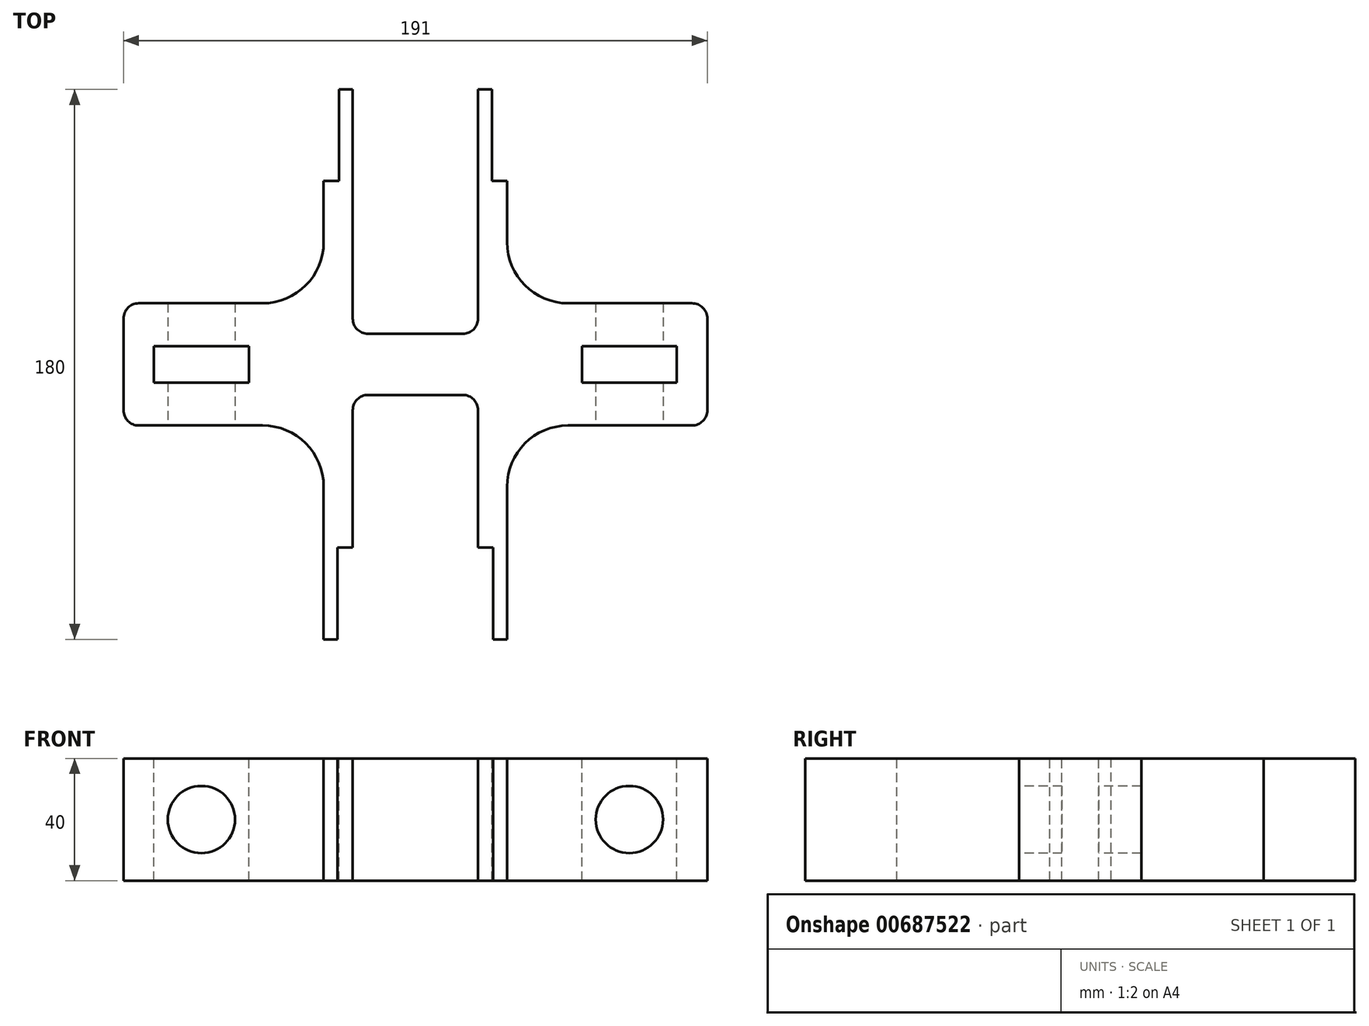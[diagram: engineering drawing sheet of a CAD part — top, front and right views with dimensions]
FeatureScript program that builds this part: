
annotation { "Feature Type Name" : "Feature", "Feature Type Description" : "" }
export const myFeature = defineFeature(function(context is Context, id is Id, definition is map)
    precondition{}
    {
        {
            var Q0;
            Q0=qCreatedBy(makeId("Front.planeOp"),FACE);
            var sketch = newSketch(context, id + "F0", { "sketchPlane" : qUnion([Q0])});
            skLineSegment(sketch, "E0.bottom", {"start": v(30, 20) * mm, "end": v(-30, 20) * mm});
            skLineSegment(sketch, "E0.top", {"start": v(30, -20) * mm, "end": v(-30, -20) * mm});
            skLineSegment(sketch, "E0.left", {"start": v(30, 20) * mm, "end": v(30, -20) * mm});
            skLineSegment(sketch, "E0.right", {"start": v(-30, 20) * mm, "end": v(-30, -20) * mm});
            skPoint(sketch, "E0.middle", {"position": v(0, 0) * mm});
            skSolve(sketch);
        }
        {
            var Q0;
            Q0 = qSketchRegion(id + "F0", true);
            extrude(context, id + "F1", {"entities" : qUnion([Q0]), "endBound" : BoundingType.SYMMETRIC, "depth" : 180 * mm, "offsetDistance" : 25 * mm});
        }
        {
            var Q0;
            Q0=makeQuery(id+"F1.opExtrude","CAP_FACE",FACE,{"disambiguationData":[OSD([sQuery(id+"F0.wireOp",EDGE,"E0.bottom"),sQuery(id+"F0.wireOp",EDGE,"E0.top"),sQuery(id+"F0.wireOp",EDGE,"E0.left"),sQuery(id+"F0.wireOp",EDGE,"E0.right")])],"isStart":false});
            var sketch = newSketch(context, id + "F2", { "sketchPlane" : qUnion([Q0])});
            skLineSegment(sketch, "E1.bottom", {"start": v(20.5, -20) * mm, "end": v(-20.5, -20) * mm});
            skLineSegment(sketch, "E1.top", {"start": v(20.5, 20) * mm, "end": v(-20.5, 20) * mm});
            skLineSegment(sketch, "E1.left", {"start": v(20.5, -20) * mm, "end": v(20.5, 20) * mm});
            skLineSegment(sketch, "E1.right", {"start": v(-20.5, -20) * mm, "end": v(-20.5, 20) * mm});
            skPoint(sketch, "E1.middle", {"position": v(0, 0) * mm});
            skSolve(sketch);
        }
        {
            var Q0;
            Q0 = qSketchRegion(id + "F2", true);
            extrude(context, id + "F3", {"entities" : qUnion([Q0]), "operationType" : NewBodyOperationType.REMOVE, "oppositeDirection" : true, "depth" : 80 * mm, "offsetDistance" : 25 * mm});
        }
        {
            var Q0;
            Q0=makeQuery(id+"F1.opExtrude","CAP_FACE",FACE,{"disambiguationData":[OSD([sQuery(id+"F0.wireOp",EDGE,"E0.bottom"),sQuery(id+"F0.wireOp",EDGE,"E0.top"),sQuery(id+"F0.wireOp",EDGE,"E0.left"),sQuery(id+"F0.wireOp",EDGE,"E0.right")])],"isStart":true});
            var sketch = newSketch(context, id + "F4", { "sketchPlane" : qUnion([Q0])});
            skLineSegment(sketch, "E2.bottom", {"start": v(-20.5, 20) * mm, "end": v(20.5, 20) * mm});
            skLineSegment(sketch, "E2.top", {"start": v(-20.5, -20) * mm, "end": v(20.5, -20) * mm});
            skLineSegment(sketch, "E2.left", {"start": v(-20.5, 20) * mm, "end": v(-20.5, -20) * mm});
            skLineSegment(sketch, "E2.right", {"start": v(20.5, 20) * mm, "end": v(20.5, -20) * mm});
            skPoint(sketch, "E2.middle", {"position": v(0, 0) * mm});
            skSolve(sketch);
        }
        {
            var Q0;
            Q0 = qSketchRegion(id + "F4", true);
            extrude(context, id + "F5", {"entities" : qUnion([Q0]), "operationType" : NewBodyOperationType.REMOVE, "oppositeDirection" : true, "depth" : 80 * mm, "offsetDistance" : 25 * mm});
        }
        {
            var Q0;
            Q0=qCreatedBy(makeId("Front.planeOp"),FACE);
            var sketch = newSketch(context, id + "F6", { "sketchPlane" : qUnion([Q0])});
            skPoint(sketch, "E3", {"position": v(70, 0) * mm});
            skLineSegment(sketch, "E4.bottom", {"start": v(20.5, -20) * mm, "end": v(95.5, -20) * mm});
            skLineSegment(sketch, "E4.top", {"start": v(20.5, 20) * mm, "end": v(95.5, 20) * mm});
            skLineSegment(sketch, "E4.left", {"start": v(20.5, -20) * mm, "end": v(20.5, 20) * mm});
            skLineSegment(sketch, "E4.right", {"start": v(95.5, -20) * mm, "end": v(95.5, 20) * mm});
            skLineSegment(sketch, "E5.bottom", {"start": v(-20.5, -20) * mm, "end": v(-95.5, -20) * mm});
            skLineSegment(sketch, "E5.top", {"start": v(-20.5, 20) * mm, "end": v(-95.5, 20) * mm});
            skLineSegment(sketch, "E5.left", {"start": v(-20.5, -20) * mm, "end": v(-20.5, 20) * mm});
            skLineSegment(sketch, "E5.right", {"start": v(-95.5, -20) * mm, "end": v(-95.5, 20) * mm});
            skPoint(sketch, "E6", {"position": v(-70, 0) * mm});
            skCircle(sketch, "E7", {"center": v(70, 0) * mm, "radius": 11 * mm});
            skCircle(sketch, "E8", {"center": v(-70, 0) * mm, "radius": 11 * mm});
            skSolve(sketch);
        }
        {
            var Q0;
            Q0 = qSketchRegion(id + "F6", true);
            extrude(context, id + "F7", {"entities" : qUnion([Q0]), "operationType" : NewBodyOperationType.ADD, "endBound" : BoundingType.SYMMETRIC, "oppositeDirection" : true, "depth" : 40 * mm, "offsetDistance" : 25 * mm});
        }
        {
            var Q0;
            Q0=makeQuery(id+"F7.boolean.opBoolean","MERGE",FACE,{"derivedFrom":[makeQuery(id+"F1.opExtrude","SWEPT_FACE",FACE,{"disambiguationData":[OSD([sQuery(id+"F0.wireOp",EDGE,"E0.bottom")])]}),makeQuery(id+"F7.opExtrude","SWEPT_FACE",FACE,{"disambiguationData":[OSD([sQuery(id+"F6.wireOp",EDGE,"E4.top")])]}),makeQuery(id+"F7.opExtrude","SWEPT_FACE",FACE,{"disambiguationData":[OSD([sQuery(id+"F6.wireOp",EDGE,"E5.top")])]})]});
            var sketch = newSketch(context, id + "F8", { "sketchPlane" : qUnion([Q0])});
            skLineSegment(sketch, "E9.bottom", {"start": v(-54.5, -6) * mm, "end": v(-85.5, -6) * mm});
            skLineSegment(sketch, "E9.top", {"start": v(-54.5, 6) * mm, "end": v(-85.5, 6) * mm});
            skLineSegment(sketch, "E9.left", {"start": v(-54.5, -6) * mm, "end": v(-54.5, 6) * mm});
            skLineSegment(sketch, "E9.right", {"start": v(-85.5, -6) * mm, "end": v(-85.5, 6) * mm});
            skPoint(sketch, "E9.middle", {"position": v(-70, 0) * mm});
            skLineSegment(sketch, "E10.bottom", {"start": v(85.5, -6) * mm, "end": v(54.5, -6) * mm});
            skLineSegment(sketch, "E10.top", {"start": v(85.5, 6) * mm, "end": v(54.5, 6) * mm});
            skLineSegment(sketch, "E10.left", {"start": v(85.5, -6) * mm, "end": v(85.5, 6) * mm});
            skLineSegment(sketch, "E10.right", {"start": v(54.5, -6) * mm, "end": v(54.5, 6) * mm});
            skPoint(sketch, "E10.middle", {"position": v(70, 0) * mm});
            skSolve(sketch);
        }
        {
            var Q0;
            Q0=makeQuery(id+"F8.imprint","IMPRINT",FACE,{"disambiguationData":[TD([[makeQuery(id+"F8.imprint","IMPRINT",EDGE,{"derivedFrom":sQuery(id+"F8.wireOp",EDGE,"E10.bottom")}),-1.0]])]});
            var Q1;
            Q1=makeQuery(id+"F8.imprint","IMPRINT",FACE,{"disambiguationData":[TD([[makeQuery(id+"F8.imprint","IMPRINT",EDGE,{"derivedFrom":sQuery(id+"F8.wireOp",EDGE,"E9.bottom")}),-1.0]])]});
            extrude(context, id + "F9", {"entities" : qUnion([Q0, Q1]), "operationType" : NewBodyOperationType.REMOVE, "oppositeDirection" : true, "depth" : 40 * mm, "offsetDistance" : 25 * mm});
        }
        {
            var Q0;
            Q0=makeQuery(id+"F7.boolean.opBoolean","INTERSECT",EDGE,{"derivedFrom":[makeQuery(id+"F1.opExtrude","SWEPT_FACE",FACE,{"disambiguationData":[OSD([sQuery(id+"F0.wireOp",EDGE,"E0.right")])]}),makeQuery(id+"F7.opExtrude","CAP_FACE",FACE,{"disambiguationData":[OSD([sQuery(id+"F6.wireOp",EDGE,"E5.bottom"),sQuery(id+"F6.wireOp",EDGE,"E5.top"),sQuery(id+"F6.wireOp",EDGE,"E5.left"),sQuery(id+"F6.wireOp",EDGE,"E5.right"),sQuery(id+"F6.wireOp",EDGE,"E8")])],"isStart":true})]});
            var Q1;
            Q1=makeQuery(id+"F7.boolean.opBoolean","INTERSECT",EDGE,{"derivedFrom":[makeQuery(id+"F1.opExtrude","SWEPT_FACE",FACE,{"disambiguationData":[OSD([sQuery(id+"F0.wireOp",EDGE,"E0.left")])]}),makeQuery(id+"F7.opExtrude","CAP_FACE",FACE,{"disambiguationData":[OSD([sQuery(id+"F6.wireOp",EDGE,"E4.bottom"),sQuery(id+"F6.wireOp",EDGE,"E4.top"),sQuery(id+"F6.wireOp",EDGE,"E4.left"),sQuery(id+"F6.wireOp",EDGE,"E4.right"),sQuery(id+"F6.wireOp",EDGE,"E7")])],"isStart":true})]});
            var Q2;
            Q2=makeQuery(id+"F7.boolean.opBoolean","INTERSECT",EDGE,{"derivedFrom":[makeQuery(id+"F1.opExtrude","SWEPT_FACE",FACE,{"disambiguationData":[OSD([sQuery(id+"F0.wireOp",EDGE,"E0.right")])]}),makeQuery(id+"F7.opExtrude","CAP_FACE",FACE,{"disambiguationData":[OSD([sQuery(id+"F6.wireOp",EDGE,"E5.bottom"),sQuery(id+"F6.wireOp",EDGE,"E5.top"),sQuery(id+"F6.wireOp",EDGE,"E5.left"),sQuery(id+"F6.wireOp",EDGE,"E5.right"),sQuery(id+"F6.wireOp",EDGE,"E8")])],"isStart":false})]});
            var Q3;
            Q3=makeQuery(id+"F7.boolean.opBoolean","INTERSECT",EDGE,{"derivedFrom":[makeQuery(id+"F1.opExtrude","SWEPT_FACE",FACE,{"disambiguationData":[OSD([sQuery(id+"F0.wireOp",EDGE,"E0.left")])]}),makeQuery(id+"F7.opExtrude","CAP_FACE",FACE,{"disambiguationData":[OSD([sQuery(id+"F6.wireOp",EDGE,"E4.bottom"),sQuery(id+"F6.wireOp",EDGE,"E4.top"),sQuery(id+"F6.wireOp",EDGE,"E4.left"),sQuery(id+"F6.wireOp",EDGE,"E4.right"),sQuery(id+"F6.wireOp",EDGE,"E7")])],"isStart":false})]});
            fillet(context, id + "F10", {"entities" : qUnion([Q0, Q1, Q2, Q3]), "radius" : 20 * mm, "tangentPropagation" : true, "allowEdgeOverflow" : false});
        }
        {
            var Q0;
            Q0=makeQuery(id+"F7.opExtrude","CAP_EDGE",EDGE,{"disambiguationData":[OSD([sQuery(id+"F6.wireOp",EDGE,"E5.right")])],"isStart":false});
            var Q1;
            Q1=makeQuery(id+"F7.opExtrude","CAP_EDGE",EDGE,{"disambiguationData":[OSD([sQuery(id+"F6.wireOp",EDGE,"E5.right")])],"isStart":true});
            var Q2;
            Q2=makeQuery(id+"F7.opExtrude","CAP_EDGE",EDGE,{"disambiguationData":[OSD([sQuery(id+"F6.wireOp",EDGE,"E4.right")])],"isStart":true});
            var Q3;
            Q3=makeQuery(id+"F7.opExtrude","CAP_EDGE",EDGE,{"disambiguationData":[OSD([sQuery(id+"F6.wireOp",EDGE,"E4.right")])],"isStart":false});
            fillet(context, id + "F11", {"entities" : qUnion([Q0, Q1, Q2, Q3]), "radius" : 5 * mm, "tangentPropagation" : true, "allowEdgeOverflow" : false});
        }
        {
            var Q0;
            Q0=makeQuery(id+"F3.boolean.opBoolean","COPY",EDGE,{"derivedFrom":makeQuery(id+"F3.opExtrude","CAP_EDGE",EDGE,{"disambiguationData":[OSD([sQuery(id+"F2.wireOp",EDGE,"E1.right")])],"isStart":false})});
            var Q1;
            Q1=makeQuery(id+"F5.boolean.opBoolean","COPY",EDGE,{"derivedFrom":makeQuery(id+"F5.opExtrude","CAP_EDGE",EDGE,{"disambiguationData":[OSD([sQuery(id+"F4.wireOp",EDGE,"E2.right")])],"isStart":false})});
            var Q2;
            Q2=makeQuery(id+"F5.boolean.opBoolean","COPY",EDGE,{"derivedFrom":makeQuery(id+"F5.opExtrude","CAP_EDGE",EDGE,{"disambiguationData":[OSD([sQuery(id+"F4.wireOp",EDGE,"E2.left")])],"isStart":false})});
            var Q3;
            Q3=makeQuery(id+"F3.boolean.opBoolean","COPY",EDGE,{"derivedFrom":makeQuery(id+"F3.opExtrude","CAP_EDGE",EDGE,{"disambiguationData":[OSD([sQuery(id+"F2.wireOp",EDGE,"E1.left")])],"isStart":false})});
            fillet(context, id + "F12", {"entities" : qUnion([Q0, Q1, Q2, Q3]), "radius" : 5 * mm, "tangentPropagation" : true, "allowEdgeOverflow" : false});
        }
        {
            var Q0;
            Q0=makeQuery(id+"F7.boolean.opBoolean","MERGE",FACE,{"derivedFrom":[makeQuery(id+"F1.opExtrude","SWEPT_FACE",FACE,{"disambiguationData":[OSD([sQuery(id+"F0.wireOp",EDGE,"E0.bottom")])]}),makeQuery(id+"F7.opExtrude","SWEPT_FACE",FACE,{"disambiguationData":[OSD([sQuery(id+"F6.wireOp",EDGE,"E4.top")])]}),makeQuery(id+"F7.opExtrude","SWEPT_FACE",FACE,{"disambiguationData":[OSD([sQuery(id+"F6.wireOp",EDGE,"E5.top")])]})]});
            var sketch = newSketch(context, id + "F13", { "sketchPlane" : qUnion([Q0])});
            skLineSegment(sketch, "E11.bottom", {"start": v(-30, 90) * mm, "end": v(-25, 90) * mm});
            skLineSegment(sketch, "E11.top", {"start": v(-30, 60) * mm, "end": v(-25, 60) * mm});
            skLineSegment(sketch, "E11.left", {"start": v(-30, 90) * mm, "end": v(-30, 60) * mm});
            skLineSegment(sketch, "E11.right", {"start": v(-25, 90) * mm, "end": v(-25, 60) * mm});
            skLineSegment(sketch, "E12.bottom", {"start": v(30, 90) * mm, "end": v(25, 90) * mm});
            skLineSegment(sketch, "E12.top", {"start": v(30, 60) * mm, "end": v(25, 60) * mm});
            skLineSegment(sketch, "E12.left", {"start": v(30, 90) * mm, "end": v(30, 60) * mm});
            skLineSegment(sketch, "E12.right", {"start": v(25, 90) * mm, "end": v(25, 60) * mm});
            skLineSegment(sketch, "E13.bottom", {"start": v(-20.5, -90) * mm, "end": v(-25.5, -90) * mm});
            skLineSegment(sketch, "E13.top", {"start": v(-20.5, -60) * mm, "end": v(-25.5, -60) * mm});
            skLineSegment(sketch, "E13.left", {"start": v(-20.5, -90) * mm, "end": v(-20.5, -60) * mm});
            skLineSegment(sketch, "E13.right", {"start": v(-25.5, -90) * mm, "end": v(-25.5, -60) * mm});
            skLineSegment(sketch, "E14.bottom", {"start": v(20.5, -90) * mm, "end": v(25.5, -90) * mm});
            skLineSegment(sketch, "E14.top", {"start": v(20.5, -60) * mm, "end": v(25.5, -60) * mm});
            skLineSegment(sketch, "E14.left", {"start": v(20.5, -90) * mm, "end": v(20.5, -60) * mm});
            skLineSegment(sketch, "E14.right", {"start": v(25.5, -90) * mm, "end": v(25.5, -60) * mm});
            skSolve(sketch);
        }
        {
            var Q0;
            Q0 = qSketchRegion(id + "F13", true);
            extrude(context, id + "F14", {"entities" : qUnion([Q0]), "operationType" : NewBodyOperationType.REMOVE, "oppositeDirection" : true, "depth" : 80 * mm, "offsetDistance" : 25 * mm});
        }
    });
